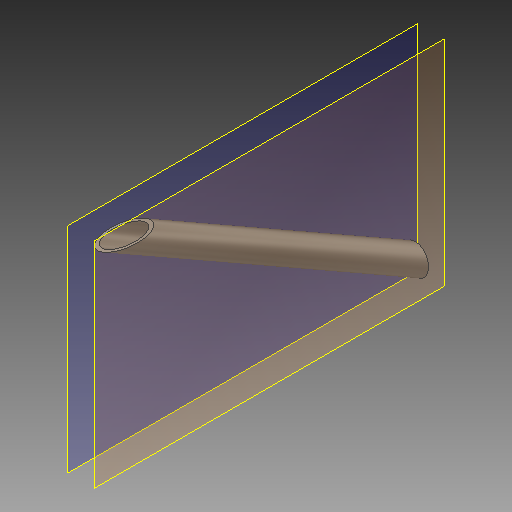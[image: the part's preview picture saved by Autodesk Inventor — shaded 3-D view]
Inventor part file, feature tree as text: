
AUTODESK INVENTOR PART (.ipt)
format: ipt  version: 2018 (Build 220112000, 112)  size: 128,512 bytes
history: native  units: mm
features: other x4, sketch x3, extrude x2, projected_geometry x1
ambient origin geometry x8: Origin, YZ Plane, XZ Plane, XY Plane, X Axis, Y Axis, Z Axis, Center Point
bodies: Body1 (feature_tree)
feature tree (10):
  other  "ソリッド1"
  sketch  "スケッチ1"
  other  "作業平面1"
  extrude  "押し出し1"  Depth=186.4mm
  extrude  "押し出し2"  Depth=326.4mm
  other  "作業平面2"
  other  "作業平面3"
  sketch  "スケッチ4"
  sketch  "スケッチ3"
  projected_geometry  "投影ループ1"
